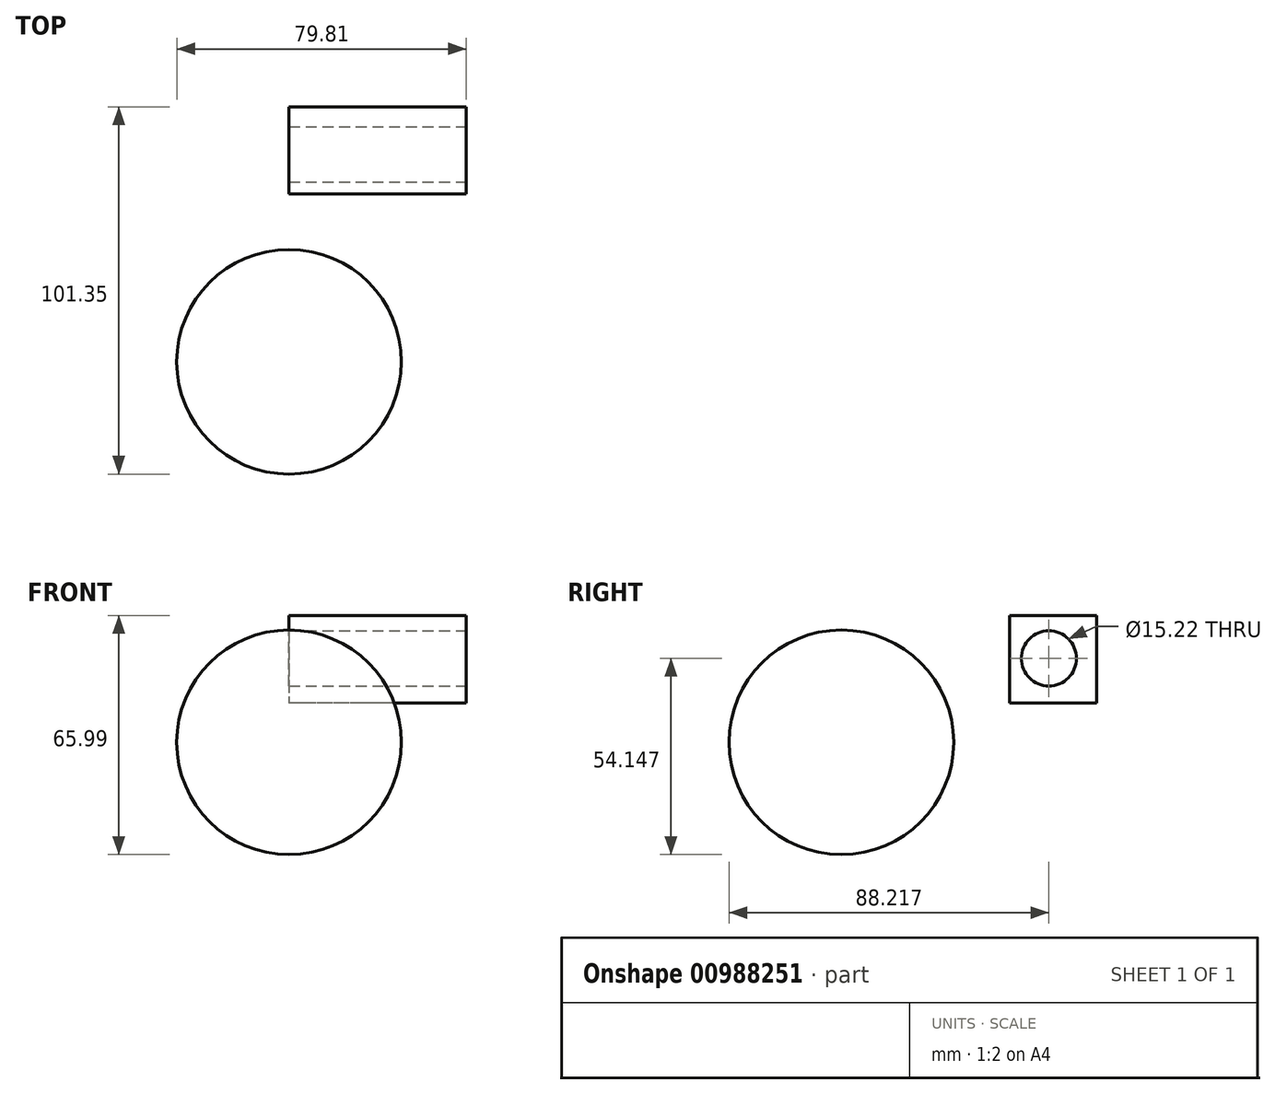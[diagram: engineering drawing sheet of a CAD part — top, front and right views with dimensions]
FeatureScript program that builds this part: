
annotation { "Feature Type Name" : "Feature", "Feature Type Description" : "" }
export const myFeature = defineFeature(function(context is Context, id is Id, definition is map)
    precondition{}
    {
        {
            var Q0;
            Q0=qCreatedBy(makeId("Right.planeOp"),FACE);
            var sketch = newSketch(context, id + "F0", { "sketchPlane" : qUnion([Q0])});
            skArc(sketch, "E0", {"start": v(0, 30.98) * mm, "mid": v(-30.98, 0) * mm, "end": v(0, -30.98) * mm});
            skLineSegment(sketch, "E1", {"start": v(48.36, 32.84) * mm, "end": v(48.36, -38.43) * mm});
            skLineSegment(sketch, "E2", {"start": v(0, 45.47) * mm, "end": v(0, -37.71) * mm});
            skSolve(sketch);
        }
        {
            var Q0;
            Q0=makeQuery(id+"F0.imprint","IMPRINT",FACE,{"disambiguationData":[TD([[makeQuery(id+"F0.imprint","IMPRINT",EDGE,{"derivedFrom":sQuery(id+"F0.wireOp",EDGE,"E0")}),1.0]])]});
            var Q1;
            Q1=sQuery(id+"F0.wireOp",EDGE,"E2");
            revolve(context, id + "F1", {"surfaceOperationType" : NewSurfaceOperationType.NEW, "entities" : qUnion([Q0]), "axis" : qUnion([Q1]), "revolveType" : RevolveType.FULL});
        }
        {
            var Q0;
            Q0=qCreatedBy(makeId("Right.planeOp"),FACE);
            var sketch = newSketch(context, id + "F2", { "sketchPlane" : qUnion([Q0])});
            skLineSegment(sketch, "E3.bottom", {"start": v(46.37, 35) * mm, "end": v(70.37, 35) * mm});
            skLineSegment(sketch, "E3.top", {"start": v(46.37, 10.83) * mm, "end": v(70.37, 10.83) * mm});
            skLineSegment(sketch, "E3.left", {"start": v(46.37, 35) * mm, "end": v(46.37, 10.83) * mm});
            skLineSegment(sketch, "E3.right", {"start": v(70.37, 35) * mm, "end": v(70.37, 10.83) * mm});
            skSolve(sketch);
        }
        {
            var Q0;
            Q0 = qSketchRegion(id + "F2", true);
            extrude(context, id + "F3", {"entities" : qUnion([Q0]), "depth" : 48.83 * mm, "offsetDistance" : 25.4 * mm});
        }
        {
            var Q0;
            Q0=makeQuery(id+"F3.opExtrude","CAP_FACE",FACE,{"disambiguationData":[OSD([sQuery(id+"F2.wireOp",EDGE,"E3.bottom"),sQuery(id+"F2.wireOp",EDGE,"E3.top"),sQuery(id+"F2.wireOp",EDGE,"E3.left"),sQuery(id+"F2.wireOp",EDGE,"E3.right")])],"isStart":false});
            var sketch = newSketch(context, id + "F4", { "sketchPlane" : qUnion([Q0])});
            skCircle(sketch, "E4", {"center": v(57.24, 23.17) * mm, "radius": 7.61 * mm});
            skSolve(sketch);
        }
        {
            var Q0;
            Q0 = qSketchRegion(id + "F4", true);
            extrude(context, id + "F5", {"entities" : qUnion([Q0]), "operationType" : NewBodyOperationType.REMOVE, "oppositeDirection" : true, "depth" : 71.6 * mm, "offsetDistance" : 25.4 * mm});
        }
    });
